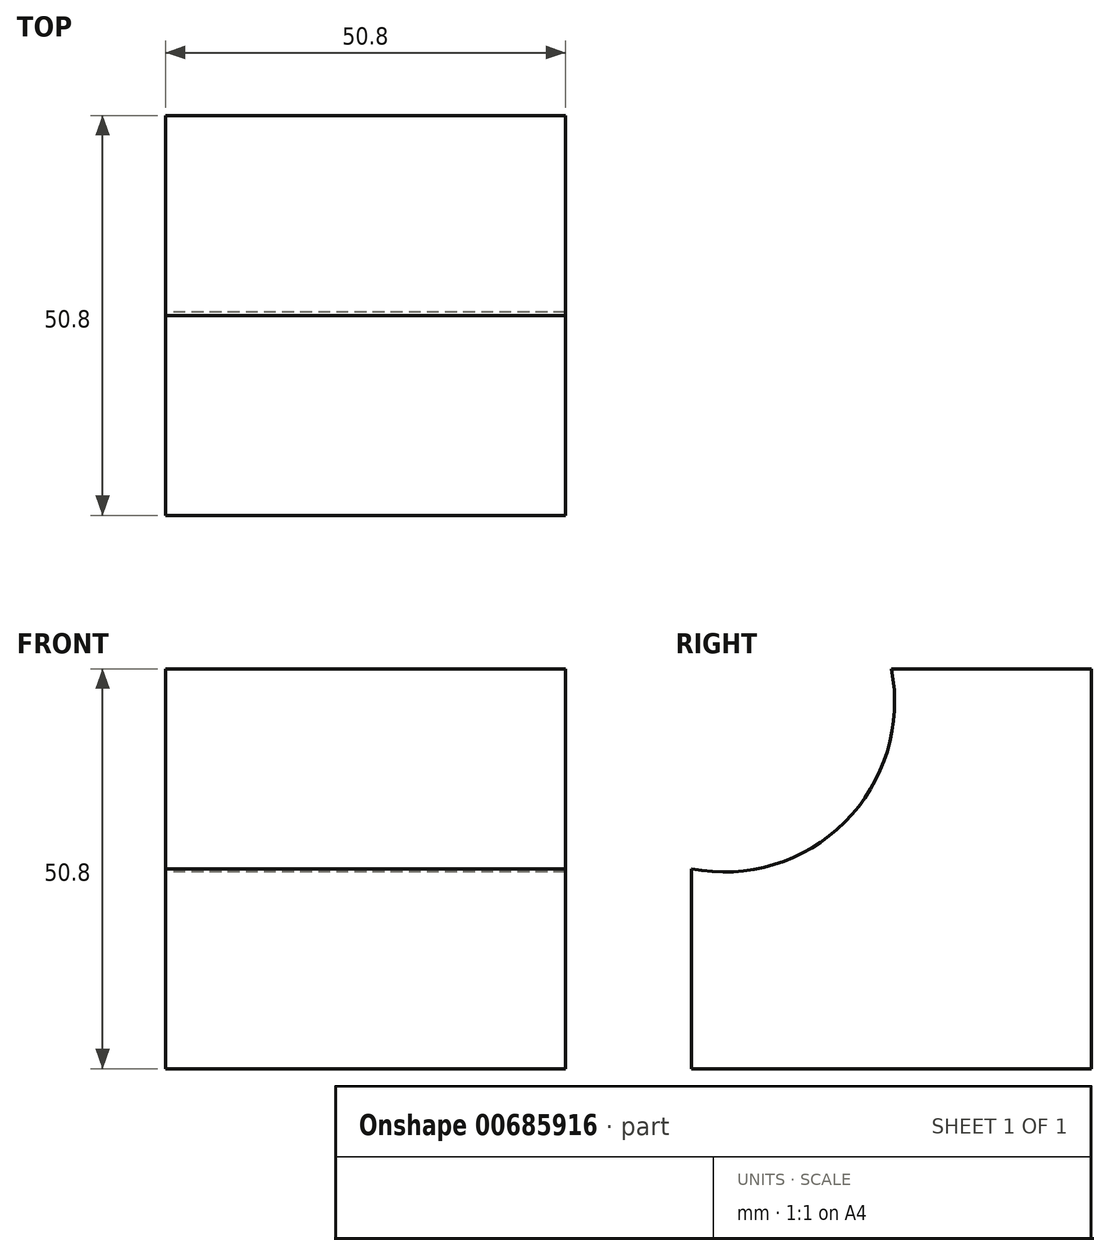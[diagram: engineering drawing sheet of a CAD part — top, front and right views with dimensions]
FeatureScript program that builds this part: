
annotation { "Feature Type Name" : "Feature", "Feature Type Description" : "" }
export const myFeature = defineFeature(function(context is Context, id is Id, definition is map)
    precondition{}
    {
        {
            var Q0;
            Q0=qCreatedBy(makeId("Right.planeOp"),FACE);
            var sketch = newSketch(context, id + "F0", { "sketchPlane" : qUnion([Q0])});
            skLineSegment(sketch, "E0", {"start": v(0, -33.9) * mm, "end": v(50.8, -33.9) * mm});
            skLineSegment(sketch, "E1", {"start": v(50.8, -33.9) * mm, "end": v(50.8, 16.9) * mm});
            skLineSegment(sketch, "E2", {"start": v(50.8, 16.9) * mm, "end": v(25.4, 16.9) * mm});
            skLineSegment(sketch, "E3", {"start": v(0, -33.9) * mm, "end": v(0, -8.5) * mm});
            skArc(sketch, "E4", {"start": v(0, -8.5) * mm, "mid": v(19.48, -2.57) * mm, "end": v(25.4, 16.9) * mm});
            skSolve(sketch);
        }
        {
            var Q0;
            Q0=makeQuery(id+"F0.imprint","IMPRINT",FACE,{"disambiguationData":[TD([[makeQuery(id+"F0.imprint","IMPRINT",EDGE,{"derivedFrom":sQuery(id+"F0.wireOp",EDGE,"E0")}),1.0]])]});
            extrude(context, id + "F1", {"entities" : qUnion([Q0]), "depth" : 50.8 * mm, "offsetDistance" : 25.4 * mm});
        }
    });
